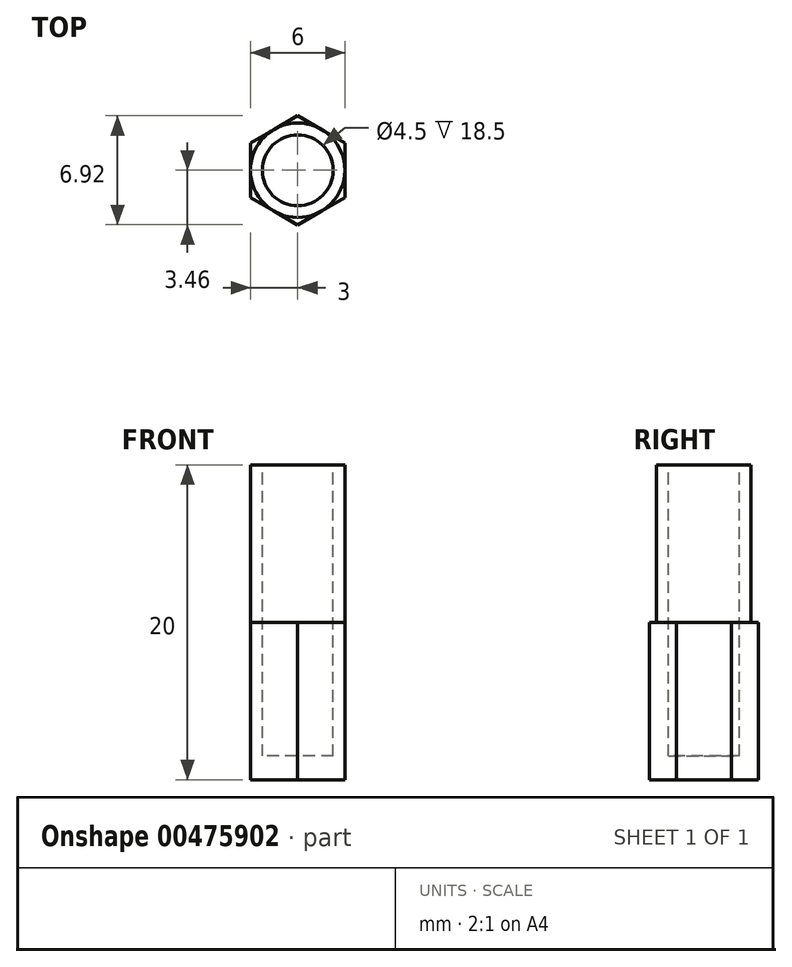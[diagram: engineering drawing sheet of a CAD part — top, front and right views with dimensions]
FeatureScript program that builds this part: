
annotation { "Feature Type Name" : "Feature", "Feature Type Description" : "" }
export const myFeature = defineFeature(function(context is Context, id is Id, definition is map)
    precondition{}
    {
        {
            var Q0;
            Q0=qCreatedBy(makeId("Top.planeOp"),FACE);
            var sketch = newSketch(context, id + "F0", { "sketchPlane" : qUnion([Q0])});
            skCircle(sketch, "E0.cCircle", {"center": v(0, 0) * mm, "radius": 3 * mm, "construction": true});
            skLineSegment(sketch, "E0.0", {"start": v(3, -1.73) * mm, "end": v(0, -3.46) * mm});
            skLineSegment(sketch, "E0.1", {"start": v(0, -3.46) * mm, "end": v(-3, -1.73) * mm});
            skLineSegment(sketch, "E0.2", {"start": v(-3, -1.73) * mm, "end": v(-3, 1.73) * mm});
            skLineSegment(sketch, "E0.3", {"start": v(-3, 1.73) * mm, "end": v(0, 3.46) * mm});
            skLineSegment(sketch, "E0.4", {"start": v(0, 3.46) * mm, "end": v(3, 1.73) * mm});
            skLineSegment(sketch, "E0.5", {"start": v(3, 1.73) * mm, "end": v(3, -1.73) * mm});
            skPoint(sketch, "E0.0.midPoint", {"position": v(1.5, -2.6) * mm});
            skSolve(sketch);
        }
        {
            var Q0;
            Q0 = qSketchRegion(id + "F0", true);
            extrude(context, id + "F1", {"entities" : qUnion([Q0]), "depth" : 20 * mm});
        }
        {
            var Q0;
            Q0=makeQuery(id+"F1.opExtrude","CAP_FACE",FACE,{"disambiguationData":[OSD([sQuery(id+"F0.wireOp",EDGE,"E0.0"),sQuery(id+"F0.wireOp",EDGE,"E0.1"),sQuery(id+"F0.wireOp",EDGE,"E0.2"),sQuery(id+"F0.wireOp",EDGE,"E0.3"),sQuery(id+"F0.wireOp",EDGE,"E0.4"),sQuery(id+"F0.wireOp",EDGE,"E0.5")])],"isStart":false});
            var sketch = newSketch(context, id + "F2", { "sketchPlane" : qUnion([Q0])});
            skCircle(sketch, "E1.0", {"center": v(0, 0) * mm, "radius": 3 * mm});
            skLineSegment(sketch, "E2.bottom", {"start": v(-4, -4) * mm, "end": v(4, -4) * mm});
            skLineSegment(sketch, "E2.top", {"start": v(-4, 4) * mm, "end": v(4, 4) * mm});
            skLineSegment(sketch, "E2.left", {"start": v(-4, -4) * mm, "end": v(-4, 4) * mm});
            skLineSegment(sketch, "E2.right", {"start": v(4, -4) * mm, "end": v(4, 4) * mm});
            skSolve(sketch);
        }
        {
            var Q0;
            Q0 = qSketchRegion(id + "F2", true);
            extrude(context, id + "F3", {"entities" : qUnion([Q0]), "operationType" : NewBodyOperationType.REMOVE, "oppositeDirection" : true, "depth" : 10 * mm});
        }
        {
            var Q0;
            Q0=makeQuery(id+"F1.opExtrude","CAP_FACE",FACE,{"disambiguationData":[OSD([sQuery(id+"F0.wireOp",EDGE,"E0.0"),sQuery(id+"F0.wireOp",EDGE,"E0.1"),sQuery(id+"F0.wireOp",EDGE,"E0.2"),sQuery(id+"F0.wireOp",EDGE,"E0.3"),sQuery(id+"F0.wireOp",EDGE,"E0.4"),sQuery(id+"F0.wireOp",EDGE,"E0.5")])],"isStart":false});
            var sketch = newSketch(context, id + "F4", { "sketchPlane" : qUnion([Q0])});
            skCircle(sketch, "E3", {"center": v(0, 0) * mm, "radius": 2.25 * mm});
            skSolve(sketch);
        }
        {
            var Q0;
            Q0=makeQuery(id+"F4.imprint","IMPRINT",FACE,{"disambiguationData":[TD([[makeQuery(id+"F4.imprint","IMPRINT",EDGE,{"derivedFrom":sQuery(id+"F4.wireOp",EDGE,"E3")}),1.0]])]});
            var Q1;
            Q1=sQuery(id+"F4.wireOp",EDGE,"E3");
            extrude(context, id + "F5", {"entities" : qUnion([Q0]), "operationType" : NewBodyOperationType.REMOVE, "surfaceEntities" : qUnion([Q1]), "oppositeDirection" : true, "depth" : 18.5 * mm});
        }
    });
